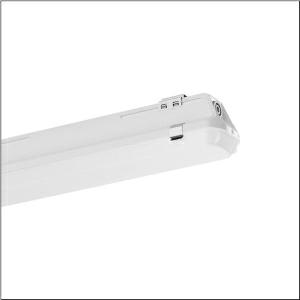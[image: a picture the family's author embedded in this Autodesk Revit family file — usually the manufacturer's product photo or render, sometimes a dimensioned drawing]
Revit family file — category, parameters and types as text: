
# Revit family: monsun_r__21_51fb10mp680b_ab58
name_source: partatom
category: Lighting Fixtures
units: mm (PartAtom-declared; Revit-internal decimal feet)

## family parameters
Cut with Voids When Loaded = No
Host = Face
Light Source = No
Part Type = Normal
Room Calculation Point = No
Round Connector Dimension = Use Diameter
Shared = No

## types (1)
- --- (1 x LED, 8190 lm, 53.6 W, 6500K)
    Apparent Load = 54 VA
    CIE Flux Codes = 47 77 93 94 100
    Color Rendering = 80
    Color Temperature = 6500K
    Default Elevation = 1800 mm
    Description = Monsun® 21, damp-proof luminaire, chain hanger, primary optical cover: enclosure, of PMMA, light emission: direct distribution, primary light characteristic: symmetric, installation type: suspended mounting, surface-mounted, horizontal mounting, vertical mounting, LED, rated luminous flux: 8.190lm, luminous efficacy: 153lm/W, light colour: 865, colour temperature: 6500K, control gear: ECG, with terminal, 3-pole, max. 2.5mm², mains connection: 220..240V, AC, 50/60Hz, rated input power: 54W, housing, of glass-fibre reinforced polyester, uncoated, bright grey, incl. chain hanger, length: 1.590mm, width: 90mm, height: 88mm, clip for enclosure, of stainless steel (V2A), ceiling mounting element, of stainless steel (V2A), chain hanger, of stainless steel (V2A), protection rating (complete): IP66, insulation class (complete): insulation class I (protective earthing), certification: CE, ENEC, VDE, UKCA, protection symbol: D, impact resistance: IK04, permissible operating ambient temperature: -25..+35°C, standard: EN 50419, EN 60598-2-1, corresponds to IFS (International Featured Standards) requirements for safety and quality in the food industry, for indoor or canopied outdoor use, no direct snow, no direct sun, no direct rain, contact your sales advisor before using the luminaires in applications with unclear chemical exposure, large temperature fluctuations or condensation-forming humidity, LABS conformity tested according to VDMA 24364:2018-05, packaging unit: 1 piece
    Height = 89 mm
    Lamp = 1 x LED
    Lamp Light Flux = 8190 lm
    Lamp Power = 53.6 W
    Lamp count = 1
    Length = 1590 mm
    Luminous efficacy = 153 lm/W
    Manufacturer = Siteco
    ModVariant = No
    Model = 51FB10MP680B
    Mounting Place = Ceiling
    Mounting Type = Surface mounted
    Number of Poles = 1
    OnlyDefault = Yes
    Power Factor = 1
    Product Name = Monsun® 21
    Product group = damp-proof luminaire
    ProductGroupID = 300
    Protection Class = Protection class I
    Protection Degree = IP 66
    RLX_Detail_Level = 1
    RLX_Emergency_Light_Flux = 0 lm
    RLX_Emergency_Type = 0
    RLX_Emergency_Type_DB = No
    RlxData = <blob elided: 89941 chars, md5=1ccc82eb>
    Socket = socket
    Standby Power = 0 W
    System Light Flux = 8190 lm
    System Power = 54 W
    Type Comments = factory setting: luminous flux: 100 % | (A | C | E) | 121 mA
    Type Image = l_1006717.jpg
    URL = http://relux.com
    VarID = @adj_079293
    Voltage = 0 V
    Weight = 0.00 kg
    Width = 90 mm

## geometry (parser evidence)
native form markers: Blend x4, Sweep x13
no freeform markers — native parametric forms only
